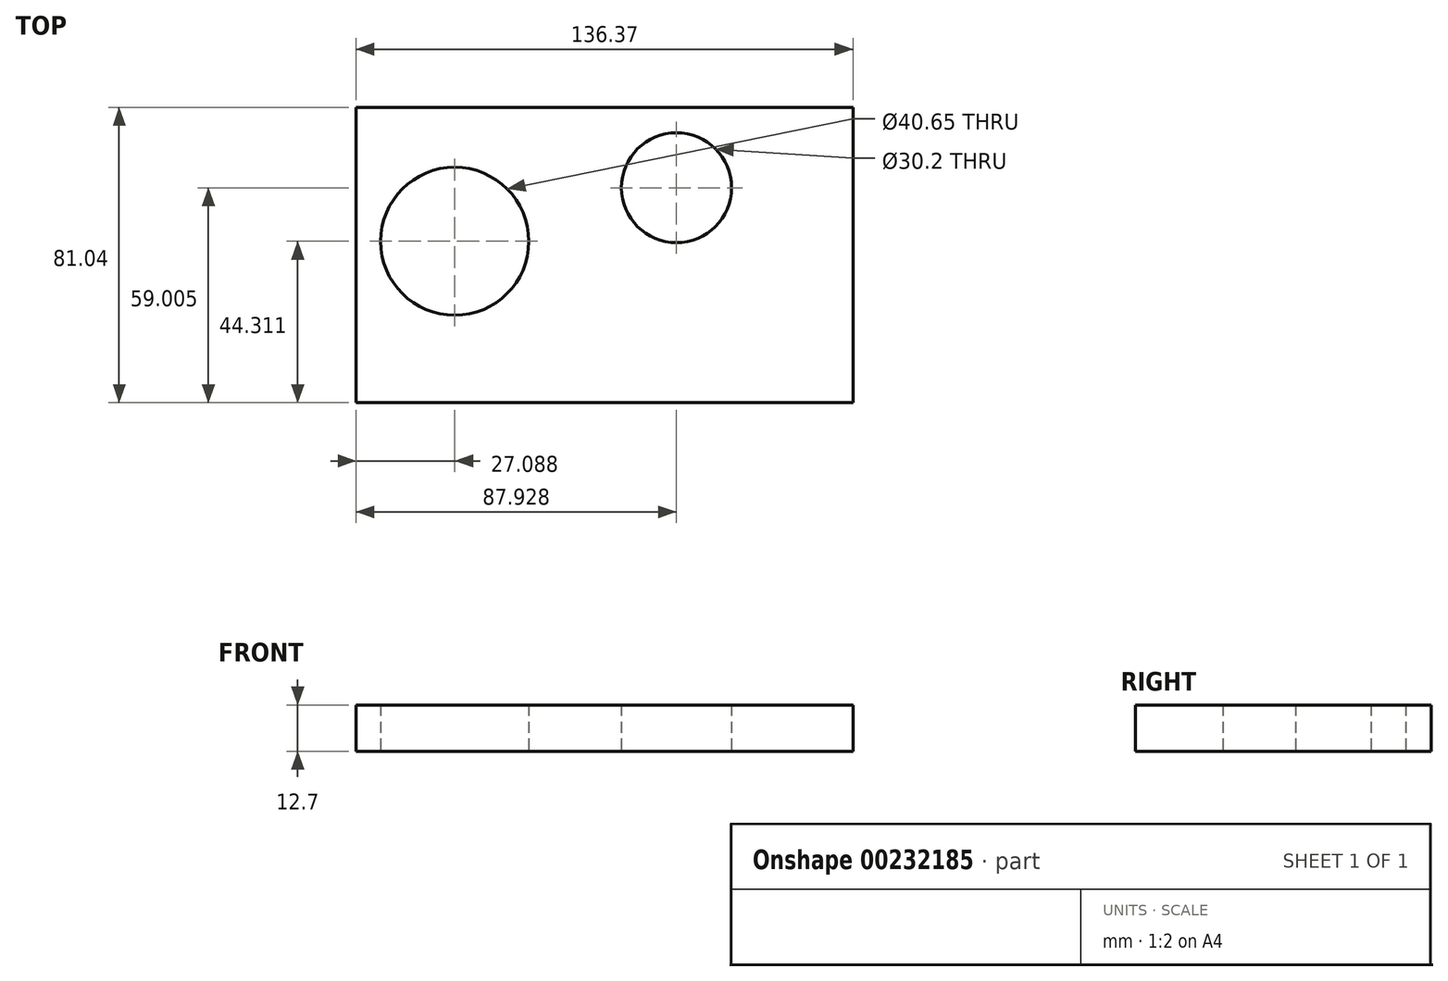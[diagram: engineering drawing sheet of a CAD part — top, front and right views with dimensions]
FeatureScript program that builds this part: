
annotation { "Feature Type Name" : "Feature", "Feature Type Description" : "" }
export const myFeature = defineFeature(function(context is Context, id is Id, definition is map)
    precondition{}
    {
        {
            var Q0;
            Q0=qCreatedBy(makeId("Top.planeOp"),FACE);
            var sketch = newSketch(context, id + "F0", { "sketchPlane" : qUnion([Q0])});
            skLineSegment(sketch, "E0.bottom", {"start": v(-64.74, 27.66) * mm, "end": v(71.63, 27.66) * mm});
            skLineSegment(sketch, "E0.top", {"start": v(-64.74, -53.38) * mm, "end": v(71.63, -53.38) * mm});
            skLineSegment(sketch, "E0.left", {"start": v(-64.74, 27.66) * mm, "end": v(-64.74, -53.38) * mm});
            skLineSegment(sketch, "E0.right", {"start": v(71.63, 27.66) * mm, "end": v(71.63, -53.38) * mm});
            skCircle(sketch, "E1", {"center": v(-37.65, -9.07) * mm, "radius": 20.32 * mm});
            skCircle(sketch, "E2", {"center": v(23.19, 5.62) * mm, "radius": 15.1 * mm});
            skSolve(sketch);
        }
        {
            var Q0;
            Q0=makeQuery(id+"F0.imprint","IMPRINT",FACE,{"disambiguationData":[TD([[makeQuery(id+"F0.imprint","IMPRINT",EDGE,{"derivedFrom":sQuery(id+"F0.wireOp",EDGE,"E0.bottom")}),-1.0]])]});
            extrude(context, id + "F1", {"entities" : qUnion([Q0]), "depth" : 12.7 * mm});
        }
    });
